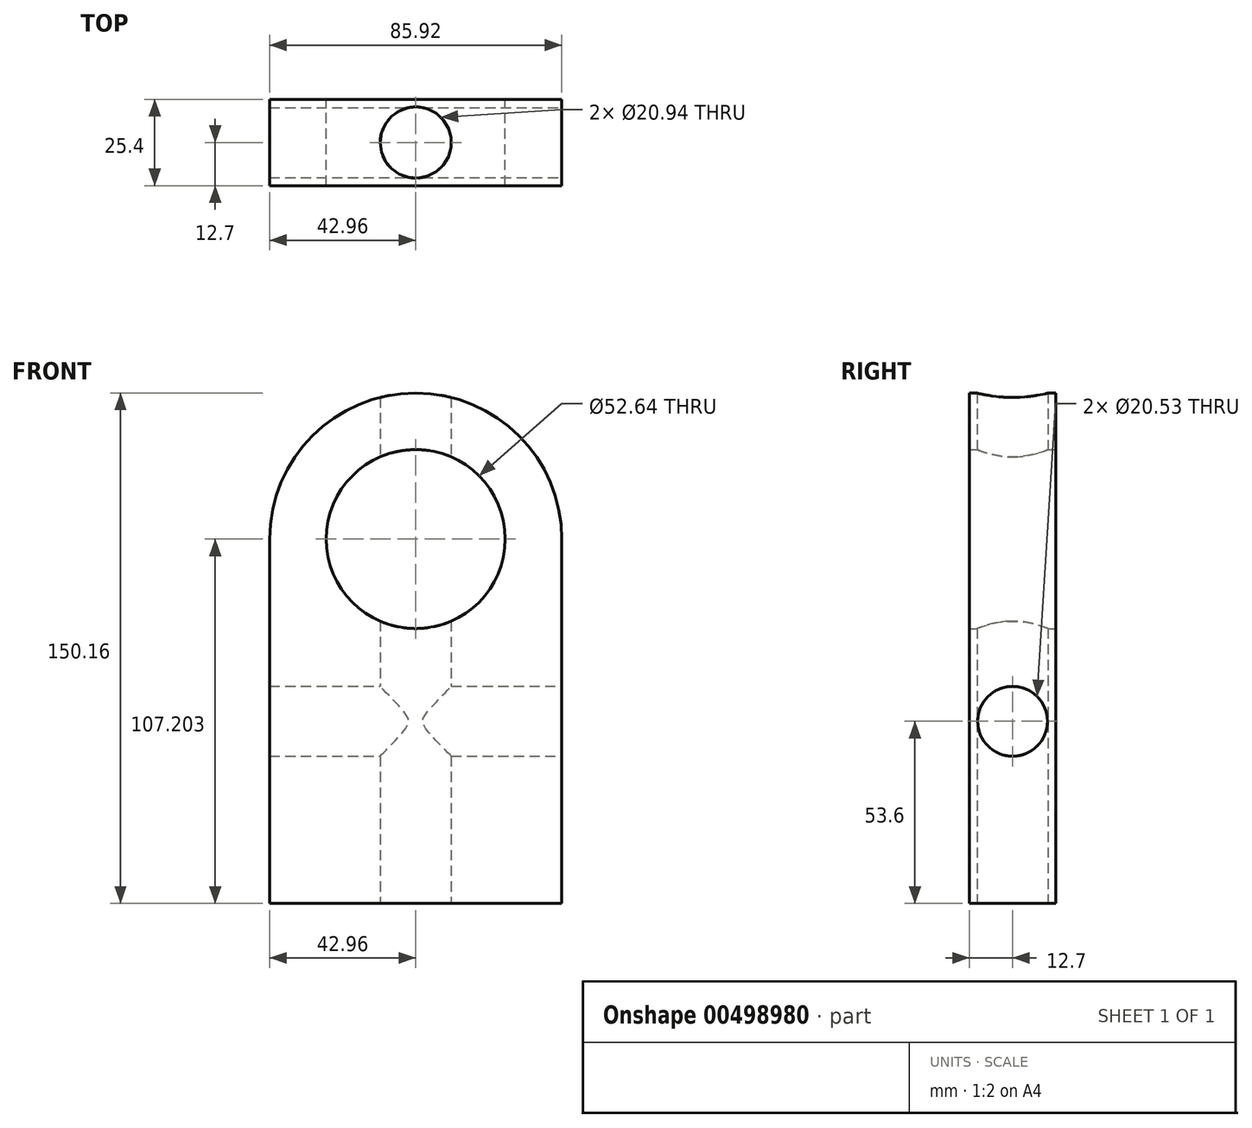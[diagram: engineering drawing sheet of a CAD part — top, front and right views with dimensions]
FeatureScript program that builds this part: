
annotation { "Feature Type Name" : "Feature", "Feature Type Description" : "" }
export const myFeature = defineFeature(function(context is Context, id is Id, definition is map)
    precondition{}
    {
        {
            var Q0;
            Q0=qCreatedBy(makeId("Front.planeOp"),FACE);
            var sketch = newSketch(context, id + "F0", { "sketchPlane" : qUnion([Q0])});
            skLineSegment(sketch, "E0.bottom", {"start": v(42.96, -53.6) * mm, "end": v(-42.96, -53.6) * mm});
            skLineSegment(sketch, "E0.left", {"start": v(42.96, -53.6) * mm, "end": v(42.96, 53.6) * mm});
            skLineSegment(sketch, "E0.right", {"start": v(-42.96, -53.6) * mm, "end": v(-42.96, 53.6) * mm});
            skPoint(sketch, "E0.middle", {"position": v(0, 0) * mm});
            skArc(sketch, "E1", {"start": v(42.96, 53.6) * mm, "mid": v(0, 96.56) * mm, "end": v(-42.96, 53.6) * mm});
            skCircle(sketch, "E2", {"center": v(0, 53.6) * mm, "radius": 26.32 * mm});
            skSolve(sketch);
        }
        {
            var Q0;
            Q0=makeQuery(id+"F0.imprint","IMPRINT",FACE,{"disambiguationData":[TD([[makeQuery(id+"F0.imprint","IMPRINT",EDGE,{"derivedFrom":sQuery(id+"F0.wireOp",EDGE,"E0.bottom")}),-1.0]])]});
            extrude(context, id + "F1", {"entities" : qUnion([Q0]), "endBound" : BoundingType.SYMMETRIC, "depth" : 25.4 * mm, "offsetDistance" : 25.4 * mm});
        }
        {
            var Q0;
            Q0=makeQuery(id+"F1.opExtrude","SWEPT_FACE",FACE,{"disambiguationData":[OSD([sQuery(id+"F0.wireOp",EDGE,"E0.bottom")])]});
            var sketch = newSketch(context, id + "F2", { "sketchPlane" : qUnion([Q0])});
            skCircle(sketch, "E3", {"center": v(0, 0) * mm, "radius": 10.47 * mm});
            skSolve(sketch);
        }
        {
            var Q0;
            Q0=makeQuery(id+"F2.imprint","IMPRINT",FACE,{"disambiguationData":[TD([[makeQuery(id+"F2.imprint","IMPRINT",EDGE,{"derivedFrom":sQuery(id+"F2.wireOp",EDGE,"E3")}),1.0]])]});
            var Q1;
            Q1=makeQuery(id+"F1.opExtrude","SWEPT_BODY",BODY,{"disambiguationData":[OSD([sQuery(id+"F0.wireOp",EDGE,"E0.bottom"),sQuery(id+"F0.wireOp",EDGE,"E0.left"),sQuery(id+"F0.wireOp",EDGE,"E0.right"),sQuery(id+"F0.wireOp",EDGE,"E1"),sQuery(id+"F0.wireOp",EDGE,"E2")])]});
            extrude(context, id + "F3", {"entities" : qUnion([Q0]), "operationType" : NewBodyOperationType.REMOVE, "endBound" : BoundingType.THROUGH_ALL, "oppositeDirection" : true, "depth" : 164.85 * mm, "endBoundEntityBody" : qUnion([Q1]), "offsetDistance" : 25.4 * mm});
        }
        {
            var Q0;
            Q0=makeQuery(id+"F1.opExtrude","SWEPT_FACE",FACE,{"disambiguationData":[OSD([sQuery(id+"F0.wireOp",EDGE,"E0.left")])]});
            var sketch = newSketch(context, id + "F4", { "sketchPlane" : qUnion([Q0])});
            skCircle(sketch, "E4", {"center": v(0, 0) * mm, "radius": 10.27 * mm});
            skSolve(sketch);
        }
        {
            var Q0;
            Q0=makeQuery(id+"F4.imprint","IMPRINT",FACE,{"disambiguationData":[TD([[makeQuery(id+"F4.imprint","IMPRINT",EDGE,{"derivedFrom":sQuery(id+"F4.wireOp",EDGE,"E4")}),1.0]])]});
            extrude(context, id + "F5", {"entities" : qUnion([Q0]), "operationType" : NewBodyOperationType.REMOVE, "endBound" : BoundingType.THROUGH_ALL, "oppositeDirection" : true, "depth" : 25.4 * mm, "offsetDistance" : 25.4 * mm});
        }
    });
